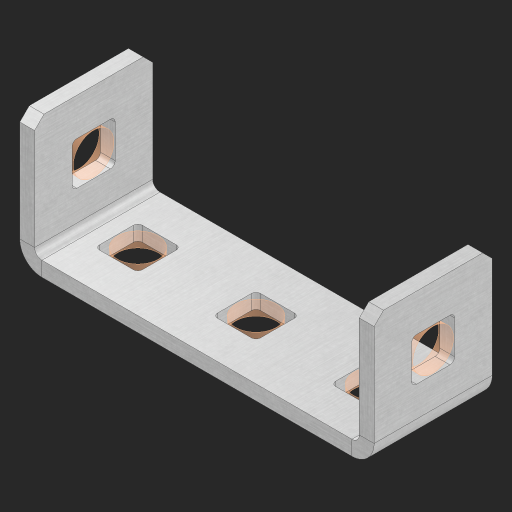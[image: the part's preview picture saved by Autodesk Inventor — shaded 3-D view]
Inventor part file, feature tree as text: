
AUTODESK INVENTOR PART (.ipt)
format: ipt  version: 2023 (Build 270158000, 158)  size: 479,232 bytes
history: native  units: in
note: dims shown in document units (in); Inventor stores cm internally (conversion verified against a paired STEP export)
features: other x10, sheet_metal_op x10, sketch x8, extrude x4, mirror x1, pattern_linear x1, chamfer x1
ambient origin geometry x8: Origin, YZ Plane, XZ Plane, XY Plane, X Axis, Y Axis, Z Axis, Center Point
bodies: Solid1 (feature_tree), Body (feature_tree)
feature tree (35):
  other  "Flange Pattern Plane"
  sheet_metal_op  "Flange Pattern"
  sheet_metal_op  "Body Pattern"
  other  "Arc Length"
  mirror  "Notch Mirror"
  pattern_linear  "Notch Pattern"  Spacing1=0.25in  [1 undecoded]
  chamfer  "End Chamfer"
  extrude  "Half Cut"  Depth=0.0625in
  sketch  "Sketch1"  dims[d0=1.5in]
  other  "Plate1"
  sketch  "Sketch2"  dims[d1=0.5in]
  other  "Plate2"
  sheet_metal_op  "Bend1"
  sheet_metal_op  "Corner1"
  sketch  "Sketch3"  dims[d2=0.0625in]
  other  "Flange Pattern Sketch"
  sketch  "Sketch7"  dims[d3=0.0625in]
  other  "Srf1"
  other  "Srf2"
  sketch  "Sketch8"  dims[d4=0.0312in]
  sketch  "Sketch9"  dims[d5=0.125in]
  other  "Srf91"
  sheet_metal_op  "Body Pattern Sketch"
  other  "Srf92"
  sketch  "Sketch13"  dims[d6=0.0625in]
  sketch  "Sketch14"  dims[d7=0.5in d8=90.0deg d9=0.0312in d10=0.25in d11=0.0625in d12=0.0625in d16=0.182in d17=0.02in d18=0.0625in d19=0.0in d20=0.25in d21=0.25in d46=0.172in d47=1.0in d48=0.0in d49=0.182in d50=0.02in d51=0.25in d52=0.25in d53=0.0625in d54=0.0in d55=0.172in d56=1.0in d57=0.0in d60=0.3937in d62=0.5in d63=1.1811in d65=0.5in d85=0.1473in d86=0.1782in d88=0.04in d89=0.0625in d90=0.0in d91=0.04in d92=0.0491in d95=2.5in d96=0.04in d97=0.25in d98=45.0deg d101=0.0in d102=2.497in d131=1.5in d132=0.3937in d134=0.5in]
  other  "Srf856"
  sheet_metal_op  "Flange Stamp"
  sheet_metal_op  "Flange Circle"
  sheet_metal_op  "Body Stamp"
  sheet_metal_op  "Body Circle"
  sheet_metal_op  "Notch"
  extrude  "ExtrusionSrf2"  Depth=0.0625in
  extrude  "ExtrusionSrf92"  Depth=0.182in
  extrude  "ExtrusionSrf856"  Depth=0.02in
note: 1 required parameter value undecoded (feature->parameter linkage not recoverable at this tier; creation-order binding heuristic only, values carry confidence <= 0.55)
